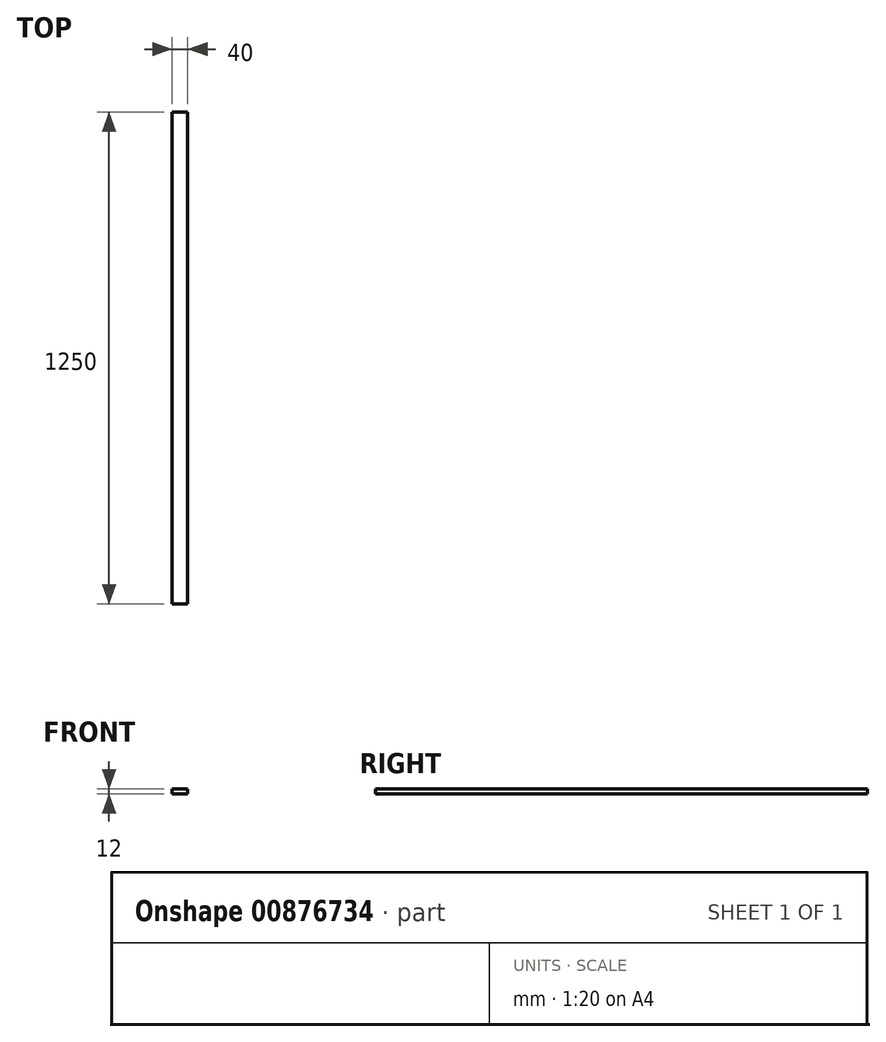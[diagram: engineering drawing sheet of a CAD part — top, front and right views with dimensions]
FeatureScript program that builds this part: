
annotation { "Feature Type Name" : "Feature", "Feature Type Description" : "" }
export const myFeature = defineFeature(function(context is Context, id is Id, definition is map)
    precondition{}
    {
        {
            var Q0;
            Q0=qCreatedBy(makeId("Front.planeOp"),FACE);
            var sketch = newSketch(context, id + "F0", { "sketchPlane" : qUnion([Q0])});
            skLineSegment(sketch, "E0.bottom", {"start": v(20, 6) * mm, "end": v(-20, 6) * mm});
            skLineSegment(sketch, "E0.top", {"start": v(20, -6) * mm, "end": v(-20, -6) * mm});
            skLineSegment(sketch, "E0.left", {"start": v(20, 6) * mm, "end": v(20, -6) * mm});
            skLineSegment(sketch, "E0.right", {"start": v(-20, 6) * mm, "end": v(-20, -6) * mm});
            skPoint(sketch, "E0.middle", {"position": v(0, 0) * mm});
            skSolve(sketch);
        }
        {
            var Q0;
            Q0=makeQuery(id+"F0.imprint","IMPRINT",FACE,{"disambiguationData":[TD([[makeQuery(id+"F0.imprint","IMPRINT",EDGE,{"derivedFrom":sQuery(id+"F0.wireOp",EDGE,"E0.bottom")}),1.0]])]});
            extrude(context, id + "F1", {"entities" : qUnion([Q0]), "depth" : 1250 * mm, "offsetDistance" : 25 * mm});
        }
    });
